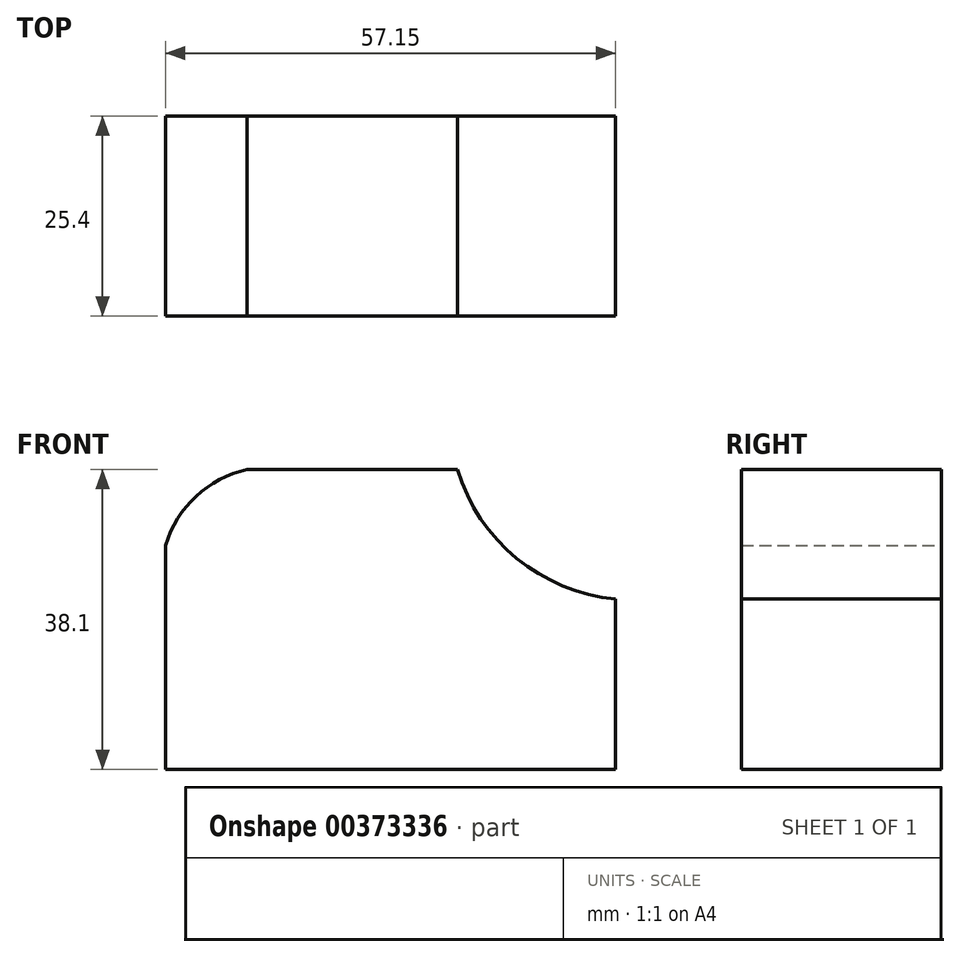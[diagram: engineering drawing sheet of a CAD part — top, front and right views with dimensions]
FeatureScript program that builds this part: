
annotation { "Feature Type Name" : "Feature", "Feature Type Description" : "" }
export const myFeature = defineFeature(function(context is Context, id is Id, definition is map)
    precondition{}
    {
        {
            var Q0;
            Q0=qCreatedBy(makeId("Front.planeOp"),FACE);
            var sketch = newSketch(context, id + "F0", { "sketchPlane" : qUnion([Q0])});
            skLineSegment(sketch, "E0", {"start": v(0, 38.1) * mm, "end": v(0, 0) * mm});
            skLineSegment(sketch, "E1", {"start": v(0, 0) * mm, "end": v(57.15, 0) * mm});
            skLineSegment(sketch, "E2", {"start": v(57.15, 0) * mm, "end": v(57.15, 38.1) * mm});
            skLineSegment(sketch, "E3", {"start": v(57.15, 38.1) * mm, "end": v(0, 38.1) * mm});
            skArc(sketch, "E4", {"start": v(10.35, 38.1) * mm, "mid": v(3.86, 34.69) * mm, "end": v(0, 28.46) * mm});
            skSolve(sketch);
        }
        {
            var Q0;
            {var subQ3=sQuery(id+"F0.wireOp",EDGE,"E1");Q0=makeQuery(id+"F0.imprint","IMPRINT",FACE,{"disambiguationData":[TD([[makeQuery(id+"F0.imprint","IMPRINT",EDGE,{"derivedFrom":subQ3}),1.0]])]});}
            extrude(context, id + "F1", {"entities" : qUnion([Q0]), "depth" : 25.4 * mm});
        }
        {
            var Q0;
            Q0=makeQuery(id+"F1.opExtrude","CAP_FACE",FACE,{"disambiguationData":[OSD([sQuery(id+"F0.wireOp",EDGE,"E0"),sQuery(id+"F0.wireOp",EDGE,"E1"),sQuery(id+"F0.wireOp",EDGE,"E2"),sQuery(id+"F0.wireOp",EDGE,"E3"),sQuery(id+"F0.wireOp",EDGE,"E4")])],"isStart":false});
            var sketch = newSketch(context, id + "F2", { "sketchPlane" : qUnion([Q0])});
            skArc(sketch, "E5", {"start": v(37.06, 38.1) * mm, "mid": v(44.6, 26.82) * mm, "end": v(57.15, 21.63) * mm});
            skSolve(sketch);
        }
        {
            var Q0;
            {var subQ0=sQuery(id+"F2.wireOp",EDGE,"E5");Q0=makeQuery(id+"F2.imprint","IMPRINT",FACE,{"disambiguationData":[TD([[makeQuery(id+"F2.imprint","IMPRINT",EDGE,{"derivedFrom":subQ0}),1.0]])]});}
            extrude(context, id + "F3", {"entities" : qUnion([Q0]), "operationType" : NewBodyOperationType.REMOVE, "oppositeDirection" : true, "depth" : 25.4 * mm});
        }
    });
